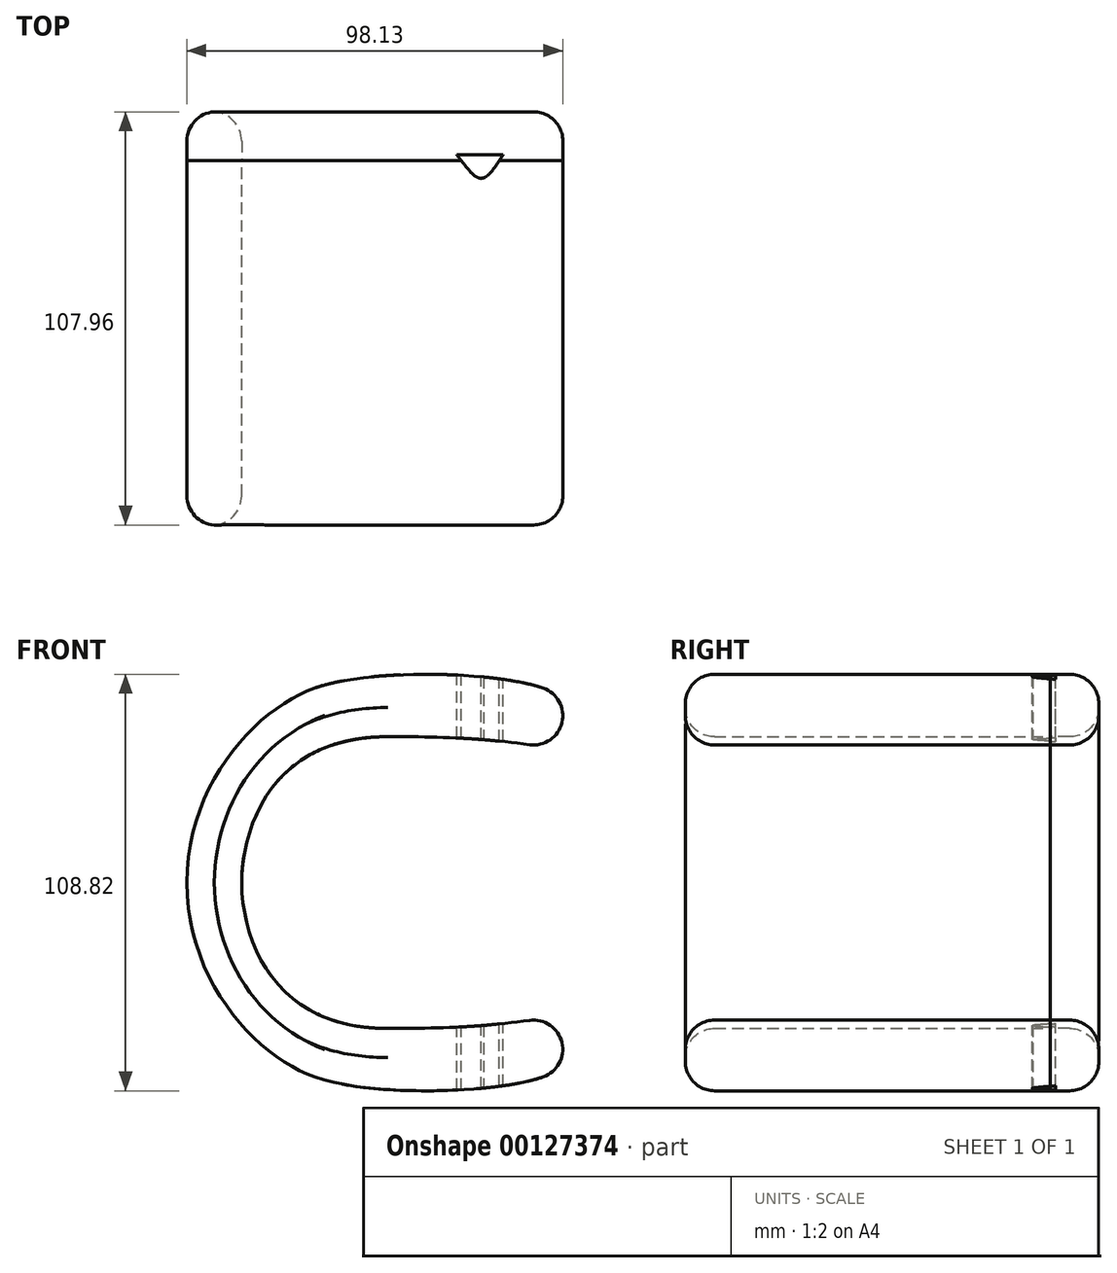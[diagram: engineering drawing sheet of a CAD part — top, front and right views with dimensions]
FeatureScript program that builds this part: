
annotation { "Feature Type Name" : "Feature", "Feature Type Description" : "" }
export const myFeature = defineFeature(function(context is Context, id is Id, definition is map)
    precondition{}
    {
        {
            var Q0;
            Q0=qCreatedBy(makeId("Front.planeOp"),FACE);
            var sketch = newSketch(context, id + "F0", { "sketchPlane" : qUnion([Q0])});
            skEllipticalArc(sketch, "E0", {"construction": true});
            skPoint(sketch, "E1", {"position": v(0, -53.97) * mm});
            skLineSegment(sketch, "E2", {"start": v(-36.51, 0) * mm, "end": v(39.69, 0) * mm, "construction": true});
            skPoint(sketch, "E3", {"position": v(-17.46, 50.8) * mm});
            skPoint(sketch, "E4", {"position": v(-50.8, 0) * mm});
            skPoint(sketch, "E5", {"position": v(50.8, 0) * mm});
            skFitSpline(sketch, "E6", {"points": [v(-17.46, 50.8) * mm, v(-50.8, 0) * mm], "startDerivative": vector(-44.91, -15.84) * mm, "endDerivative": vector(0, -78.25) * mm});
            skLineSegment(sketch, "E7", {"start": v(-17.46, 50.8) * mm, "end": v(-32.43, 45.52) * mm, "construction": true});
            skPoint(sketch, "E8", {"position": v(1.59, 0) * mm});
            skLineSegment(sketch, "E9.bottom", {"start": v(-17.46, 50.8) * mm, "end": v(42.18, 50.8) * mm, "construction": true});
            skLineSegment(sketch, "E9.top", {"start": v(-17.46, 38.1) * mm, "end": v(42.18, 38.1) * mm, "construction": true});
            skLineSegment(sketch, "E9.left", {"start": v(-17.46, 50.8) * mm, "end": v(-17.46, 38.1) * mm, "construction": true});
            skPoint(sketch, "E10", {"position": v(0, 53.97) * mm});
            skFitSpline(sketch, "E11", {"points": [v(-36.51, 0) * mm, v(1.59, 38.1) * mm], "startDerivative": vector(0, 36.27) * mm, "endDerivative": vector(95.48, 0) * mm});
            skFitSpline(sketch, "E12", {"points": [v(-17.46, 50.8) * mm, v(42.18, 50.8) * mm], "startDerivative": vector(44.91, 15.84) * mm, "endDerivative": vector(37.63, -12.98) * mm});
            skLineSegment(sketch, "E13", {"start": v(-2.5, 56.08) * mm, "end": v(-17.46, 50.8) * mm, "construction": true});
            skFitSpline(sketch, "E14", {"points": [v(1.59, 38.1) * mm, v(38.66, 36) * mm], "startDerivative": vector(32.31, 0) * mm, "endDerivative": vector(46.2, -6.27) * mm});
            skLineSegment(sketch, "E15", {"start": v(115.18, 25.62) * mm, "end": v(29.64, 55.13) * mm, "construction": true});
            skLineSegment(sketch, "E16", {"start": v(23.26, 38.1) * mm, "end": v(115.18, 25.62) * mm, "construction": true});
            skArc(sketch, "E17", {"start": v(42.18, 50.8) * mm, "mid": v(47.12, 41.8) * mm, "end": v(38.66, 36) * mm});
            skFitSpline(sketch, "E18.MirrorCS", {"points": [v(-36.51, 0) * mm, v(1.59, -38.1) * mm], "startDerivative": vector(0, -36.27) * mm, "endDerivative": vector(95.48, 0) * mm});
            skFitSpline(sketch, "E19.MirrorCS", {"points": [v(1.59, -38.1) * mm, v(38.66, -36) * mm], "startDerivative": vector(32.31, 0) * mm, "endDerivative": vector(46.2, 6.27) * mm});
            skArc(sketch, "E20.MirrorCS", {"start": v(42.18, -50.8) * mm, "mid": v(47.12, -41.8) * mm, "end": v(38.66, -36) * mm});
            skFitSpline(sketch, "E21.MirrorCS", {"points": [v(-17.46, -50.8) * mm, v(42.18, -50.8) * mm], "startDerivative": vector(44.91, -15.84) * mm, "endDerivative": vector(37.63, 12.98) * mm});
            skFitSpline(sketch, "E22.MirrorCS", {"points": [v(-17.46, -50.8) * mm, v(-50.8, 0) * mm], "startDerivative": vector(-44.91, 15.84) * mm, "endDerivative": vector(0, 78.25) * mm});
            skLineSegment(sketch, "E23", {"start": v(-64.56, 34.92) * mm, "end": v(-64.56, -34.93) * mm, "construction": true});
            skPoint(sketch, "E24", {"position": v(-64.56, 0) * mm});
            skLineSegment(sketch, "E25", {"start": v(-64.56, 34.92) * mm, "end": v(-38.43, 34.92) * mm, "construction": true});
            skLineSegment(sketch, "E26", {"start": v(-38.43, 34.92) * mm, "end": v(-38.43, 50.8) * mm, "construction": true});
            skLineSegment(sketch, "E27", {"start": v(-38.43, 34.92) * mm, "end": v(-38.43, 24.53) * mm, "construction": true});
            skPoint(sketch, "E28", {"position": v(12.36, 50.8) * mm});
            skPoint(sketch, "E29", {"position": v(12.36, 54.41) * mm});
            skLineSegment(sketch, "E30", {"start": v(12.36, 64.67) * mm, "end": v(12.36, -23.83) * mm, "construction": true});
            skLineSegment(sketch, "E31", {"start": v(-36.51, 12.1) * mm, "end": v(-36.51, -12.1) * mm, "construction": true});
            skLineSegment(sketch, "E32", {"start": v(-50.8, 26.08) * mm, "end": v(-50.8, -26.08) * mm, "construction": true});
            skEllipticalArc(sketch, "E33.trimOffspring", {"construction": true});
            skLineSegment(sketch, "E34", {"start": v(42.18, 50.8) * mm, "end": v(42.18, 38.1) * mm, "construction": true});
            skLineSegment(sketch, "E35", {"start": v(-30.24, 38.1) * mm, "end": v(-50.8, 0) * mm, "construction": true});
            skEllipticalArc(sketch, "E36.trimOffspring", {"construction": true});
            skPoint(sketch, "E37", {"position": v(-17.46, 34.02) * mm});
            const initialGuessF0  = {"E0": [0, 0, 0, 1, 0.053975, 0.0508, 3.141592653589793, 4.71238898038469], "E33.trimOffspring": [0, 0, 0, 1, 0.053975, 0.0508, 0.8578198344051552, 0.8670758187116736], "E36.trimOffspring": [0, 0, 0, 1, 0.053975, 0.0508, 5.445808340624176, 5.445858286037961]};
            skSetInitialGuess(sketch, initialGuessF0);
            skSolve(sketch);
        }
        {
            var Q0;
            Q0 = qSketchRegion(id + "F0", true);
            extrude(context, id + "F1", {"entities" : qUnion([Q0]), "endBound" : BoundingType.SYMMETRIC, "depth" : 95.25 * mm});
        }
        {
            var Q0;
            Q0=makeQuery(id+"F1.opExtrude","CAP_FACE",FACE,{"disambiguationData":[OSD([sQuery(id+"F0.wireOp",EDGE,"E6"),sQuery(id+"F0.wireOp",EDGE,"E11"),sQuery(id+"F0.wireOp",EDGE,"E12"),sQuery(id+"F0.wireOp",EDGE,"E14"),sQuery(id+"F0.wireOp",EDGE,"E17"),sQuery(id+"F0.wireOp",EDGE,"E18.MirrorCS"),sQuery(id+"F0.wireOp",EDGE,"E19.MirrorCS"),sQuery(id+"F0.wireOp",EDGE,"E20.MirrorCS"),sQuery(id+"F0.wireOp",EDGE,"E21.MirrorCS"),sQuery(id+"F0.wireOp",EDGE,"E22.MirrorCS")])],"isStart":false});
            var sketch = newSketch(context, id + "F2", { "sketchPlane" : qUnion([Q0])});
            skFitSpline(sketch, "E38.0", {"points": [v(-36.51, 0) * mm, v(-36.51, 12.1) * mm, v(-30.24, 38.1) * mm, v(1.59, 38.1) * mm]});
            skPoint(sketch, "E39", {"position": v(1.59, 19.05) * mm});
            skLineSegment(sketch, "E40", {"start": v(1.59, 19.05) * mm, "end": v(-32.06, 19.05) * mm, "construction": true});
            skFitSpline(sketch, "E41.0", {"points": [v(-36.51, 0) * mm, v(-36.51, -12.1) * mm, v(-30.24, -38.1) * mm, v(1.59, -38.1) * mm]});
            skFitSpline(sketch, "E41.1", {"points": [v(1.59, -38.1) * mm, v(12.57, -38.1) * mm, v(23.26, -38.1) * mm, v(38.66, -36) * mm]});
            skFitSpline(sketch, "E41.2", {"points": [v(-17.46, -50.8) * mm, v(-32.43, -45.52) * mm, v(-50.8, -26.08) * mm, v(-50.8, 0) * mm]});
            skPoint(sketch, "E42", {"position": v(-32.06, 19.05) * mm});
            skPoint(sketch, "E43", {"position": v(-26.99, -45.78) * mm});
            skArc(sketch, "E44", {"start": v(-32.06, 19.05) * mm, "mid": v(-36.5, 0.7) * mm, "end": v(-32.67, -17.78) * mm});
            skArc(sketch, "E45", {"start": v(-32.06, 19.05) * mm, "mid": v(-35.39, 9.78) * mm, "end": v(-36.51, 0) * mm});
            skLineSegment(sketch, "E46", {"start": v(1.59, -38.1) * mm, "end": v(1.59, -54.1) * mm, "construction": true});
            skLineSegment(sketch, "E47", {"start": v(1.59, -54.1) * mm, "end": v(1.59, -89.34) * mm, "construction": true});
            skLineSegment(sketch, "E48", {"start": v(-26.99, -82.99) * mm, "end": v(-26.99, -52.13) * mm});
            skLineSegment(sketch, "E49", {"start": v(17.46, -89.34) * mm, "end": v(-20.64, -89.34) * mm});
            skLineSegment(sketch, "E50", {"start": v(-20.64, -45.78) * mm, "end": v(30.16, -45.78) * mm});
            skFitSpline(sketch, "E51.0", {"points": [v(-17.46, -50.8) * mm, v(-2.5, -56.08) * mm, v(29.64, -55.13) * mm, v(42.18, -50.8) * mm]});
            skPoint(sketch, "E52", {"position": v(11.57, -54.41) * mm});
            skArc(sketch, "E53.filletArc", {"start": v(-20.64, -45.78) * mm, "mid": v(-25.13, -47.64) * mm, "end": v(-26.99, -52.13) * mm});
            skLineSegment(sketch, "E54", {"start": v(-17.46, -50.8) * mm, "end": v(17.46, -50.8) * mm});
            skArc(sketch, "E55.0", {"start": v(42.18, -50.8) * mm, "mid": v(47.12, -41.8) * mm, "end": v(38.66, -36) * mm});
            skLineSegment(sketch, "E56", {"start": v(47.33, -39.13) * mm, "end": v(47.33, -61.51) * mm});
            skLineSegment(sketch, "E57", {"start": v(-36.51, -54.41) * mm, "end": v(23.81, -54.41) * mm, "construction": true});
            skLineSegment(sketch, "E58", {"start": v(-17.46, -50.8) * mm, "end": v(-17.46, -45.78) * mm});
            skPoint(sketch, "E59.visualSharp", {"position": v(-26.99, -89.34) * mm});
            skArc(sketch, "E59.filletArc", {"start": v(-26.99, -82.99) * mm, "mid": v(-25.13, -87.48) * mm, "end": v(-20.64, -89.34) * mm});
            skPoint(sketch, "E60", {"position": v(23.81, -89.34) * mm});
            skLineSegment(sketch, "E61", {"start": v(23.81, -57.15) * mm, "end": v(23.81, -82.99) * mm});
            skPoint(sketch, "E62.visualSharp", {"position": v(23.81, -50.8) * mm});
            skArc(sketch, "E62.filletArc", {"start": v(23.81, -57.15) * mm, "mid": v(21.95, -52.66) * mm, "end": v(17.46, -50.8) * mm});
            skPoint(sketch, "E63.orphan", {"position": v(30.16, -89.34) * mm});
            skArc(sketch, "E64.filletArc", {"start": v(17.46, -89.34) * mm, "mid": v(21.95, -87.48) * mm, "end": v(23.81, -82.99) * mm});
            skPoint(sketch, "E65.5.internal.snap0", {"position": v(-25.13, -47.64) * mm});
            skPoint(sketch, "E65.6.internal.snap0", {"position": v(-25.13, -47.64) * mm});
            skLineSegment(sketch, "E66", {"start": v(-82.55, -54.41) * mm, "end": v(47.12, -54.41) * mm, "construction": true});
            skPoint(sketch, "E66.endSnap0", {"position": v(47.12, -41.8) * mm});
            skLineSegment(sketch, "E67", {"start": v(-36.51, 0) * mm, "end": v(-50.8, 0) * mm});
            skLineSegment(sketch, "E68", {"start": v(-36.51, 0) * mm, "end": v(-36.51, 38.1) * mm});
            skPoint(sketch, "E69", {"position": v(-36.51, 37.2) * mm});
            skLineSegment(sketch, "E70", {"start": v(72.14, 38.1) * mm, "end": v(-35.7, 38.1) * mm, "construction": true});
            skLineSegment(sketch, "E71", {"start": v(-36.51, 0) * mm, "end": v(-36.51, -37.2) * mm});
            skArc(sketch, "E72", {"start": v(-36.51, 0) * mm, "mid": v(-35.54, -9.1) * mm, "end": v(-32.67, -17.78) * mm});
            skArc(sketch, "E73.MirrorCS", {"start": v(-32.06, -19.05) * mm, "mid": v(-35.39, -9.78) * mm, "end": v(-36.51, 0) * mm});
            skFitSpline(sketch, "E74.0", {"points": [v(-17.46, 50.8) * mm, v(-32.43, 45.52) * mm, v(-50.8, 26.08) * mm, v(-50.8, 0) * mm]});
            skFitSpline(sketch, "E75", {"points": [v(-17.46, 50.8) * mm, v(-32.43, 45.52) * mm, v(-50.8, 26.08) * mm, v(-50.8, 0) * mm]});
            skLineSegment(sketch, "E76", {"start": v(-32.06, 19.05) * mm, "end": v(-47.39, 19.05) * mm});
            skFitSpline(sketch, "E77", {"points": [v(-17.46, 50.8) * mm, v(-32.43, 45.52) * mm, v(-50.8, 26.08) * mm, v(-50.8, 0) * mm]});
            skLineSegment(sketch, "E78", {"start": v(-29.17, 24.91) * mm, "end": v(-32.06, 19.05) * mm, "construction": true});
            skFitSpline(sketch, "E79", {"points": [v(-36.51, 37.2) * mm, v(-32.06, 19.05) * mm], "startDerivative": vector(19.6, -27.02) * mm, "endDerivative": vector(-8.69, -17.59) * mm});
            skFitSpline(sketch, "E80", {"points": [v(-17.46, -50.8) * mm, v(-32.43, -45.52) * mm, v(-50.8, -26.08) * mm, v(-50.8, 0) * mm]});
            skFitSpline(sketch, "E81.0", {"points": [v(-17.46, 50.8) * mm, v(-32.43, 45.52) * mm, v(-50.8, 26.08) * mm, v(-50.8, 0) * mm]});
            skLineSegment(sketch, "E82", {"start": v(1.59, 38.1) * mm, "end": v(1.59, -38.1) * mm, "construction": true});
            skLineSegment(sketch, "E83", {"start": v(-36.51, 0) * mm, "end": v(1.59, 0) * mm, "construction": true});
            skLineSegment(sketch, "E84", {"start": v(-36.51, 37.2) * mm, "end": v(-29.98, 28.2) * mm, "construction": true});
            skLineSegment(sketch, "E85", {"start": v(-29.98, 28.2) * mm, "end": v(-29.17, 24.91) * mm, "construction": true});
            skFitSpline(sketch, "E86.MirrorCS", {"points": [v(-36.51, -37.2) * mm, v(-32.06, -19.05) * mm], "startDerivative": vector(19.6, 27.02) * mm, "endDerivative": vector(-8.69, 17.59) * mm});
            skLineSegment(sketch, "E87", {"start": v(-36.51, 37.2) * mm, "end": v(-22.91, 47.07) * mm, "construction": true});
            skLineSegment(sketch, "E88", {"start": v(-47.39, 19.05) * mm, "end": v(-79.14, 19.05) * mm, "construction": true});
            skLineSegment(sketch, "E89", {"start": v(-36.51, 37.2) * mm, "end": v(-68.26, 37.2) * mm, "construction": true});
            skLineSegment(sketch, "E90", {"start": v(-79.14, 19.05) * mm, "end": v(-79.14, 37.2) * mm, "construction": true});
            skLineSegment(sketch, "E91", {"start": v(-79.14, 37.2) * mm, "end": v(-68.26, 37.2) * mm, "construction": true});
            skLineSegment(sketch, "E92", {"start": v(-68.26, 37.2) * mm, "end": v(-68.26, 50.8) * mm, "construction": true});
            skPoint(sketch, "E93", {"position": v(-68.26, 44) * mm});
            skPoint(sketch, "E94", {"position": v(-79.14, 28.13) * mm});
            skPoint(sketch, "E95", {"position": v(-52.39, 37.2) * mm});
            skLineSegment(sketch, "E96", {"start": v(-68.26, 50.8) * mm, "end": v(-17.46, 50.8) * mm, "construction": true});
            skFitSpline(sketch, "E97", {"points": [v(-17.46, 50.8) * mm, v(-68.26, 37.2) * mm], "startDerivative": vector(-60.73, 0) * mm, "endDerivative": vector(-64.5, -36) * mm});
            skPoint(sketch, "E98", {"position": v(-42.86, 50.8) * mm});
            skSolve(sketch);
        }
        {
            var Q0;
            Q0=sQuery(id+"F2.wireOp",VERTEX,"E41.2.end");
            var Q1;
            Q1=qCreatedBy(makeId("Right.planeOp"),FACE);
            cPlane(context, id + "F3", {"entities" : qUnion([Q0, Q1]), "cplaneType" : CPlaneType.PLANE_POINT, "offset" : 203.2 * mm, "width" : 152.4 * mm, "height" : 152.4 * mm});
        }
        {
            var Q0;
            Q0=makeQuery(id+"F1.opExtrude","CAP_FACE",FACE,{"disambiguationData":[OSD([sQuery(id+"F0.wireOp",EDGE,"E6"),sQuery(id+"F0.wireOp",EDGE,"E11"),sQuery(id+"F0.wireOp",EDGE,"E12"),sQuery(id+"F0.wireOp",EDGE,"E14"),sQuery(id+"F0.wireOp",EDGE,"E17"),sQuery(id+"F0.wireOp",EDGE,"E18.MirrorCS"),sQuery(id+"F0.wireOp",EDGE,"E19.MirrorCS"),sQuery(id+"F0.wireOp",EDGE,"E20.MirrorCS"),sQuery(id+"F0.wireOp",EDGE,"E21.MirrorCS"),sQuery(id+"F0.wireOp",EDGE,"E22.MirrorCS")])],"isStart":true});
            extrude(context, id + "F4", {"entities" : qUnion([Q0]), "depth" : 12.7 * mm});
        }
        {
            var Q0;
            Q0=makeQuery(id+"F4.opExtrude","CAP_FACE",FACE,{"disambiguationData":[OSD([sQuery(id+"F0.wireOp",EDGE,"E6"),sQuery(id+"F0.wireOp",EDGE,"E11"),sQuery(id+"F0.wireOp",EDGE,"E12"),sQuery(id+"F0.wireOp",EDGE,"E14"),sQuery(id+"F0.wireOp",EDGE,"E17"),sQuery(id+"F0.wireOp",EDGE,"E18.MirrorCS"),sQuery(id+"F0.wireOp",EDGE,"E19.MirrorCS"),sQuery(id+"F0.wireOp",EDGE,"E20.MirrorCS"),sQuery(id+"F0.wireOp",EDGE,"E21.MirrorCS"),sQuery(id+"F0.wireOp",EDGE,"E22.MirrorCS")])],"isStart":false});
            cPlane(context, id + "F5", {"entities" : qUnion([Q0]), "cplaneType" : CPlaneType.OFFSET, "offset" : 0 * mm, "width" : 152.4 * mm, "height" : 152.4 * mm});
        }
        {
            var Q0;
            Q0=qCreatedBy(id+"F5.planeOp",FACE);
            var sketch = newSketch(context, id + "F6", { "sketchPlane" : qUnion([Q0])});
            skFitSpline(sketch, "E99.0", {"points": [v(17.46, 50.8) * mm, v(2.5, 56.08) * mm, v(-29.64, 55.13) * mm, v(-42.18, 50.8) * mm]});
            skFitSpline(sketch, "E99.1", {"points": [v(17.46, 50.8) * mm, v(32.43, 45.52) * mm, v(50.8, 26.08) * mm, v(50.8, 0) * mm]});
            skArc(sketch, "E99.2", {"start": v(-42.18, 50.8) * mm, "mid": v(-47.12, 41.8) * mm, "end": v(-38.66, 36) * mm});
            skFitSpline(sketch, "E99.3", {"points": [v(36.51, 0) * mm, v(36.51, 12.1) * mm, v(30.24, 38.1) * mm, v(-1.59, 38.1) * mm]});
            skFitSpline(sketch, "E99.4", {"points": [v(-1.59, 38.1) * mm, v(-12.57, 38.1) * mm, v(-23.26, 38.1) * mm, v(-38.66, 36) * mm]});
            skFitSpline(sketch, "E99.5", {"points": [v(17.46, -50.8) * mm, v(32.43, -45.52) * mm, v(50.8, -26.08) * mm, v(50.8, 0) * mm]});
            skFitSpline(sketch, "E99.6", {"points": [v(36.51, 0) * mm, v(36.51, -12.1) * mm, v(30.24, -38.1) * mm, v(-1.59, -38.1) * mm]});
            skFitSpline(sketch, "E99.7", {"points": [v(17.46, -50.8) * mm, v(2.5, -56.08) * mm, v(-29.64, -55.13) * mm, v(-42.18, -50.8) * mm]});
            skArc(sketch, "E99.8", {"start": v(-42.18, -50.8) * mm, "mid": v(-47.12, -41.8) * mm, "end": v(-38.66, -36) * mm});
            skFitSpline(sketch, "E99.9", {"points": [v(-1.59, -38.1) * mm, v(-12.57, -38.1) * mm, v(-23.26, -38.1) * mm, v(-38.66, -36) * mm]});
            skLineSegment(sketch, "E100.bottom", {"start": v(-42.18, 50.8) * mm, "end": v(17.46, 50.8) * mm, "construction": true});
            skLineSegment(sketch, "E100.top", {"start": v(-42.18, 38.1) * mm, "end": v(17.46, 38.1) * mm, "construction": true});
            skLineSegment(sketch, "E100.left", {"start": v(-42.18, 50.8) * mm, "end": v(-42.18, 38.1) * mm, "construction": true});
            skLineSegment(sketch, "E100.right", {"start": v(17.46, 50.8) * mm, "end": v(17.46, 38.1) * mm, "construction": true});
            skPoint(sketch, "E101", {"position": v(-12.36, 50.8) * mm});
            skPoint(sketch, "E102", {"position": v(-12.36, 54.41) * mm});
            skSolve(sketch);
        }
        {
            var Q0;
            Q0=qCreatedBy(makeId("Top.planeOp"),FACE);
            cPlane(context, id + "F7", {"entities" : qUnion([Q0]), "cplaneType" : CPlaneType.OFFSET, "offset" : 63.5 * mm, "width" : 152.4 * mm, "height" : 152.4 * mm});
        }
        {
            var Q0;
            Q0=qCreatedBy(id+"F7.planeOp",FACE);
            var sketch = newSketch(context, id + "F8", { "sketchPlane" : qUnion([Q0])});
            skLineSegment(sketch, "E103.0", {"start": v(47.33, 60.33) * mm, "end": v(38.66, 60.33) * mm});
            skFitSpline(sketch, "E104.0", {"points": [v(-17.46, 44.45) * mm, v(-2.5, 44.45) * mm, v(29.64, 44.45) * mm, v(42.18, 44.45) * mm]});
            skFitSpline(sketch, "E105.0.0", {"points": [v(-50.8, 31.75) * mm, v(-39.69, 31.75) * mm, v(-28.58, 31.75) * mm, v(-17.46, 31.75) * mm]});
            skFitSpline(sketch, "E105.0.2", {"points": [v(-17.46, 44.45) * mm, v(-28.58, 44.45) * mm, v(-39.69, 44.45) * mm, v(-50.8, 44.45) * mm]});
            skLineSegment(sketch, "E105.0.3", {"start": v(-50.8, 60.33) * mm, "end": v(-50.8, 47.63) * mm});
            skLineSegment(sketch, "E106.top", {"start": v(42.18, 60.33) * mm, "end": v(12.36, 60.33) * mm, "construction": true});
            skLineSegment(sketch, "E106.left", {"start": v(42.18, 47.63) * mm, "end": v(42.18, 53.98) * mm, "construction": true});
            skPoint(sketch, "E107.endSnap0", {"position": v(-17.46, 38.1) * mm});
            skLineSegment(sketch, "E108", {"start": v(47.33, 38.1) * mm, "end": v(47.33, 47.63) * mm});
            skLineSegment(sketch, "E109", {"start": v(47.33, 38.1) * mm, "end": v(47.33, 39.69) * mm});
            skLineSegment(sketch, "E110", {"start": v(12.36, 60.33) * mm, "end": v(-2.55, 60.33) * mm, "construction": true});
            skLineSegment(sketch, "E111", {"start": v(-2.55, 60.33) * mm, "end": v(-10, 60.32) * mm, "construction": true});
            skLineSegment(sketch, "E112", {"start": v(-10, 60.32) * mm, "end": v(-17.46, 60.32) * mm, "construction": true});
            skLineSegment(sketch, "E113", {"start": v(-17.46, -9.53) * mm, "end": v(-17.46, 25.4) * mm, "construction": true});
            skLineSegment(sketch, "E114", {"start": v(-17.46, 25.4) * mm, "end": v(-17.46, 42.86) * mm, "construction": true});
            skLineSegment(sketch, "E115", {"start": v(-17.46, 42.86) * mm, "end": v(-17.46, 60.33) * mm, "construction": true});
            skLineSegment(sketch, "E116", {"start": v(-17.46, 60.33) * mm, "end": v(-12.38, 60.33) * mm, "construction": true});
            skLineSegment(sketch, "E117", {"start": v(42.18, 60.33) * mm, "end": v(37.1, 60.33) * mm, "construction": true});
            skPoint(sketch, "E118", {"position": v(47.33, 57.42) * mm});
            skFitSpline(sketch, "E119", {"points": [v(47.33, 57.42) * mm, v(42.18, 44.17) * mm], "startDerivative": vector(0, 8.7) * mm, "endDerivative": vector(-7.08, 0) * mm});
            skLineSegment(sketch, "E120", {"start": v(47.33, 49.1) * mm, "end": v(47.33, 57.42) * mm});
            skLineSegment(sketch, "E121", {"start": v(47.33, 49.1) * mm, "end": v(-36.51, 49.1) * mm});
            skLineSegment(sketch, "E122", {"start": v(-28.43, 47.63) * mm, "end": v(-50.8, 47.63) * mm, "construction": true});
            skPoint(sketch, "E123", {"position": v(-28.43, 42.86) * mm});
            skLineSegment(sketch, "E124", {"start": v(-45.65, 49.1) * mm, "end": v(-36.51, 49.1) * mm});
            skLineSegment(sketch, "E125", {"start": v(-50.8, 43.07) * mm, "end": v(-50.8, 49.1) * mm});
            skLineSegment(sketch, "E126", {"start": v(-50.8, 49.1) * mm, "end": v(-45.65, 49.1) * mm});
            skPoint(sketch, "E127", {"position": v(-36.51, 60.33) * mm});
            skFitSpline(sketch, "E128.0", {"points": [v(-17.46, 31.75) * mm, v(-2.5, 31.75) * mm, v(29.64, 31.75) * mm, v(42.18, 31.75) * mm]});
            skPoint(sketch, "E129", {"position": v(-17.46, 47.63) * mm});
            skPoint(sketch, "E130", {"position": v(42.18, 47.63) * mm});
            skLineSegment(sketch, "E131", {"start": v(-17.46, 47.62) * mm, "end": v(42.18, 47.62) * mm, "construction": true});
            skPoint(sketch, "E132", {"position": v(12.36, 47.63) * mm});
            skLineSegment(sketch, "E133", {"start": v(12.36, 47.63) * mm, "end": v(12.36, 53.98) * mm, "construction": true});
            skPoint(sketch, "E134", {"position": v(12.36, 60.33) * mm});
            skLineSegment(sketch, "E135", {"start": v(12.36, 53.98) * mm, "end": v(12.36, 57.15) * mm, "construction": true});
            skLineSegment(sketch, "E136", {"start": v(12.36, 57.15) * mm, "end": v(12.36, 60.33) * mm, "construction": true});
            skLineSegment(sketch, "E137", {"start": v(42.18, 53.98) * mm, "end": v(42.18, 57.15) * mm, "construction": true});
            skLineSegment(sketch, "E138", {"start": v(42.18, 57.15) * mm, "end": v(42.18, 58.74) * mm, "construction": true});
            skLineSegment(sketch, "E139", {"start": v(42.18, 58.74) * mm, "end": v(42.18, 60.33) * mm, "construction": true});
            skLineSegment(sketch, "E140", {"start": v(37.1, 57.15) * mm, "end": v(12.36, 57.15) * mm, "construction": true});
            skPoint(sketch, "E141", {"position": v(37.1, 57.42) * mm});
            skPoint(sketch, "E142", {"position": v(37.1, 57.15) * mm});
            skLineSegment(sketch, "E143", {"start": v(12.36, 57.15) * mm, "end": v(-12.38, 57.15) * mm, "construction": true});
            skPoint(sketch, "E144", {"position": v(-12.38, 57.42) * mm});
            skLineSegment(sketch, "E145", {"start": v(42.18, 60.33) * mm, "end": v(40.15, 60.33) * mm, "construction": true});
            skLineSegment(sketch, "E146", {"start": v(-17.46, 60.33) * mm, "end": v(-36.51, 60.33) * mm});
            skPoint(sketch, "E147", {"position": v(-6.4, 40.9) * mm});
            skLineSegment(sketch, "E148", {"start": v(-28.43, 60.33) * mm, "end": v(-36.51, 60.33) * mm});
            skPoint(sketch, "E149", {"position": v(3.75, 57.15) * mm});
            skLineSegment(sketch, "E150.bottom", {"start": v(42.18, 60.33) * mm, "end": v(-28.43, 60.33) * mm, "construction": true});
            skLineSegment(sketch, "E150.top", {"start": v(42.18, 51.98) * mm, "end": v(-28.43, 51.98) * mm, "construction": true});
            skLineSegment(sketch, "E150.left", {"start": v(42.18, 45.03) * mm, "end": v(42.18, 51.98) * mm, "construction": true});
            skLineSegment(sketch, "E150.right", {"start": v(-28.43, 51.98) * mm, "end": v(-28.43, 60.33) * mm, "construction": true});
            skPoint(sketch, "E151", {"position": v(6.87, 51.98) * mm});
            skLineSegment(sketch, "E152.bottom", {"start": v(47.33, 60.33) * mm, "end": v(-50.8, 60.33) * mm, "construction": true});
            skLineSegment(sketch, "E152.top", {"start": v(47.33, 56.27) * mm, "end": v(-50.8, 56.27) * mm, "construction": true});
            skLineSegment(sketch, "E152.left", {"start": v(47.33, 56.27) * mm, "end": v(47.33, 60.33) * mm, "construction": true});
            skLineSegment(sketch, "E152.right", {"start": v(-50.8, 56.27) * mm, "end": v(-50.8, 60.33) * mm, "construction": true});
            skPoint(sketch, "E153", {"position": v(-16.17, 56.27) * mm});
            skPoint(sketch, "E154", {"position": v(6.87, 57.15) * mm});
            skFitSpline(sketch, "E155", {"points": [v(42.18, 60.33) * mm, v(25.99, 42.94) * mm, v(6.87, 57.15) * mm], "startDerivative": vector(-49.08, -19.22) * mm, "endDerivative": vector(-64.04, 0) * mm});
            skLineSegment(sketch, "E156", {"start": v(6.87, 46.06) * mm, "end": v(6.87, 37.1) * mm, "construction": true});
            skPoint(sketch, "E157.endSnap0", {"position": v(-50.8, 46.08) * mm});
            skFitSpline(sketch, "E158.MirrorCS", {"points": [v(-28.43, 43.64) * mm, v(-12.36, 42.96) * mm, v(6.87, 57.15) * mm], "startDerivative": vector(46.9, 0) * mm, "endDerivative": vector(63.97, 0) * mm});
            skLineSegment(sketch, "E159", {"start": v(-28.43, 43.64) * mm, "end": v(-36.51, 43.64) * mm});
            skPoint(sketch, "E160.orphan", {"position": v(-46.51, 43.64) * mm});
            skFitSpline(sketch, "E161", {"points": [v(-36.51, 43.64) * mm, v(-50.8, 42.17) * mm], "startDerivative": vector(-23.22, 0) * mm, "endDerivative": vector(0, -4.7) * mm});
            skFitSpline(sketch, "E162", {"points": [v(25.99, 42.94) * mm, v(42.18, 44.17) * mm], "startDerivative": vector(22.24, 3.7) * mm, "endDerivative": vector(24.53, 0) * mm});
            skSolve(sketch);
        }
        {
            var Q0;
            Q0=makeQuery(id+"F4.opExtrude","CAP_EDGE",EDGE,{"disambiguationData":[OSD([sQuery(id+"F0.wireOp",EDGE,"E18.MirrorCS")])],"isStart":false});
            var Q1;
            Q1=makeQuery(id+"F4.opExtrude","CAP_EDGE",EDGE,{"disambiguationData":[OSD([sQuery(id+"F0.wireOp",EDGE,"E6")])],"isStart":false});
            fillet(context, id + "F9", {"entities" : qUnion([Q0, Q1]), "radius" : 7.62 * mm, "tangentPropagation" : true, "allowEdgeOverflow" : false});
        }
        {
            var Q0;
            {var subQ0=sQuery(id+"F8.wireOp",EDGE,"E103.0");Q0=makeQuery(id+"F8.imprint","IMPRINT",FACE,{"disambiguationData":[TD([[makeQuery(id+"F8.imprint","IMPRINT",EDGE,{"derivedFrom":subQ0}),1.0]])]});}
            var Q1;
            {var subQ6=sQuery(id+"F8.wireOp",EDGE,"E103.0");Q1=makeQuery(id+"F8.imprint","IMPRINT",FACE,{"disambiguationData":[TD([[makeQuery(id+"F8.imprint","IMPRINT",EDGE,{"derivedFrom":subQ6}),-1.0]])]});}
            var Q2;
            {var subQ0=sQuery(id+"F8.wireOp",EDGE,"2698f85a-1893-4b02-8930-94dbd363c92a");Q2=makeQuery(id+"F8.imprint","IMPRINT",FACE,{"disambiguationData":[TD([[makeQuery(id+"F8.imprint","IMPRINT",EDGE,{"derivedFrom":subQ0}),-1.0]])]});}
            var Q3;
            {var subQ5=sQuery(id+"F8.wireOp",EDGE,"35b80836-bed2-4c65-bd87-0732fe959dc2");Q3=makeQuery(id+"F8.imprint","IMPRINT",FACE,{"disambiguationData":[TD([[makeQuery(id+"F8.imprint","IMPRINT",EDGE,{"derivedFrom":subQ5}),-1.0]])]});}
            var Q4;
            {var subQ5=sQuery(id+"F8.wireOp",EDGE,"11337054-a038-4a9d-a434-ef29e41be4330.MirrorCS");Q4=makeQuery(id+"F8.imprint","IMPRINT",FACE,{"disambiguationData":[TD([[makeQuery(id+"F8.imprint","IMPRINT",EDGE,{"derivedFrom":subQ5}),1.0]])]});}
            var Q5;
            {var subQ3=sQuery(id+"F8.wireOp",EDGE,"92e74fdf-f9ca-4010-b776-d4ea54654c73");Q5=makeQuery(id+"F8.imprint","IMPRINT",FACE,{"disambiguationData":[TD([[makeQuery(id+"F8.imprint","IMPRINT",EDGE,{"derivedFrom":subQ3}),-1.0]])]});}
            var Q6;
            {var subQ3=sQuery(id+"F8.wireOp",EDGE,"E146");Q6=makeQuery(id+"F8.imprint","IMPRINT",FACE,{"disambiguationData":[TD([[makeQuery(id+"F8.imprint","IMPRINT",EDGE,{"derivedFrom":subQ3}),1.0]])]});}
            var Q7;
            {var subQ4=sQuery(id+"F8.wireOp",EDGE,"E155");Q7=makeQuery(id+"F8.imprint","IMPRINT",FACE,{"disambiguationData":[TD([[makeQuery(id+"F8.imprint","IMPRINT",EDGE,{"derivedFrom":subQ4}),-1.0]])]});}
            extrude(context, id + "F10", {"entities" : qUnion([Q0, Q1, Q2, Q3, Q4, Q5, Q6, Q7]), "operationType" : NewBodyOperationType.REMOVE, "endBound" : BoundingType.THROUGH_ALL, "oppositeDirection" : true, "depth" : 50.8 * mm});
        }
        {
            var Q0;
            Q0=qCreatedBy(makeId("Front.planeOp"),FACE);
            var sketch = newSketch(context, id + "F11", { "sketchPlane" : qUnion([Q0])});
            skFitSpline(sketch, "E163.0", {"points": [v(-17.46, 50.8) * mm, v(-2.5, 56.08) * mm, v(29.64, 55.13) * mm, v(42.18, 50.8) * mm]});
            skArc(sketch, "E163.1", {"start": v(42.18, 50.8) * mm, "mid": v(47.12, 41.8) * mm, "end": v(38.66, 36) * mm});
            skFitSpline(sketch, "E163.2", {"points": [v(1.59, 38.1) * mm, v(12.57, 38.1) * mm, v(23.26, 38.1) * mm, v(38.66, 36) * mm]});
            skFitSpline(sketch, "E163.3", {"points": [v(-36.51, 0) * mm, v(-36.51, 12.1) * mm, v(-30.24, 38.1) * mm, v(1.59, 38.1) * mm]});
            skFitSpline(sketch, "E163.4", {"points": [v(-17.46, 50.8) * mm, v(-32.43, 45.52) * mm, v(-50.8, 26.08) * mm, v(-50.8, 0) * mm]});
            skLineSegment(sketch, "E163.5", {"start": v(-64.56, 34.92) * mm, "end": v(-64.56, -34.93) * mm});
            skLineSegment(sketch, "E163.6", {"start": v(-64.56, 34.92) * mm, "end": v(-38.43, 34.92) * mm});
            skPoint(sketch, "E164.orphan", {"position": v(-50.8, 0) * mm});
            skLineSegment(sketch, "E165", {"start": v(-38.43, 34.92) * mm, "end": v(-15.5, 34.92) * mm, "construction": true});
            skPoint(sketch, "E166.orphan", {"position": v(-36.51, 0) * mm});
            skLineSegment(sketch, "E167", {"start": v(-50.8, 0) * mm, "end": v(-50.8, 19.48) * mm, "construction": true});
            skLineSegment(sketch, "E168", {"start": v(-34.19, 54.41) * mm, "end": v(59.15, 54.41) * mm, "construction": true});
            skPoint(sketch, "E169", {"position": v(11.57, 54.41) * mm});
            skFitSpline(sketch, "E170.0", {"points": [v(-36.51, 0) * mm, v(-36.51, 12.1) * mm, v(-30.24, 38.1) * mm, v(1.59, 38.1) * mm]});
            skLineSegment(sketch, "E171", {"start": v(-50.8, 19.48) * mm, "end": v(-31.85, 19.48) * mm, "construction": true});
            skSolve(sketch);
        }
        {
            var Q0;
            Q0=makeQuery(id+"F1.opExtrude","CAP_EDGE",EDGE,{"disambiguationData":[OSD([sQuery(id+"F0.wireOp",EDGE,"E12")])],"isStart":false});
            fillet(context, id + "F12", {"entities" : qUnion([Q0]), "radius" : 7.62 * mm, "tangentPropagation" : true, "allowEdgeOverflow" : false});
        }
    });
